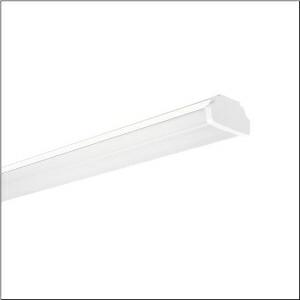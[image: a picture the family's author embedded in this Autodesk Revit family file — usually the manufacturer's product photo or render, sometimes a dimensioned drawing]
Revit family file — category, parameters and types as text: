
# Revit family: modario_31_gen_2_53bm812mv4a5c2_9e3d
name_source: partatom
category: Lighting Fixtures
units: mm (PartAtom-declared; Revit-internal decimal feet)

## family parameters
Cut with Voids When Loaded = No
Host = Face
Light Source = No
Part Type = Normal
Room Calculation Point = No
Round Connector Dimension = Use Diameter
Shared = No

## types (1)
- --- (1 x LED, 10960 lm, 60.5 W, 4000K)
    Apparent Load = 61 VA
    CIE Flux Codes = 47 80 95 93 100
    Color Rendering = 80
    Color Temperature = 4000K
    Default Elevation = 1800 mm
    Description = Modario 31 Gen.2, luminaire insert, of sheet steel, coil coated, white, length: 1.495mm, width: 81mm, height: 82mm, 5x system unit, system units: 299mm, LED rated luminous flux: 10.960lm, light colour: 840, SDCM (Standard Deviation of Colour Matching)MacAdam ≤ 3 SDCM (initial), control gear: ON/OFF Multilumen, control gear: ECG, with plug, 3-pole, with phase selection, mains connection: 220..240V, AC, 50/60Hz, rated input power: 61W, through-wiring accessed according to module size, primary optical cover: cover, of PMMA, light emission: direct distribution, primary light characteristic: symmetric, protection rating (complete): IP20, protection rating (LED compartment): IP50, insulation class (complete): insulation class I (protective earthing), certification: CE, ENEC, VDE, UKCA, impact resistance: IK03, permissible ambient temperature for indoor applications: -35..+40°C, corresponds to IFS (International Featured Standards) requirements for safety and quality in the food industry, reducing of maximum allowable ambient temperature of 5°C with ceiling mounting, IP40 when using the optional accessory 5TP9018, packaging unit: 1 piece
    Height = 92 mm
    Lamp = 1 x LED
    Lamp Light Flux = 10960 lm
    Lamp Power = 60.5 W
    Lamp count = 1
    Length = 1495 mm
    Luminous efficacy = 181 lm/W
    Manufacturer = Siteco
    ModVariant = No
    Model = 53BM812MV4A5C2
    Mounting Place = Ceiling
    Mounting Type = Pendant
    Number of Poles = 1
    OnlyDefault = Yes
    Power Factor = 1
    Product Name = Modario 31 Gen.2
    Product group = luminaire insert | ceiling pendant
    ProductGroupID = 901
    Protection Class = Protection class I
    Protection Degree = IP 20
    RLX_Detail_Level = 1
    RLX_Emergency_Light_Flux = 0 lm
    RLX_Emergency_Type = 0
    RLX_Emergency_Type_DB = No
    RlxData = <blob elided: 39977 chars, md5=19a43c8e>
    Socket = socket
    Standby Power = 0 W
    System Light Flux = 10960 lm
    System Power = 61 W
    Type Comments = factory setting: luminous flux: 100 % | (A | C | E) | 140 mA
    Type Image = l_1341886.jpg
    URL = http://relux.com
    VarID = @adj_050833
    Voltage = 0 V
    Weight = 0.00 kg
    Width = 81 mm

## geometry (parser evidence)
native form markers: Blend x4, Sweep x12
no freeform markers — native parametric forms only
